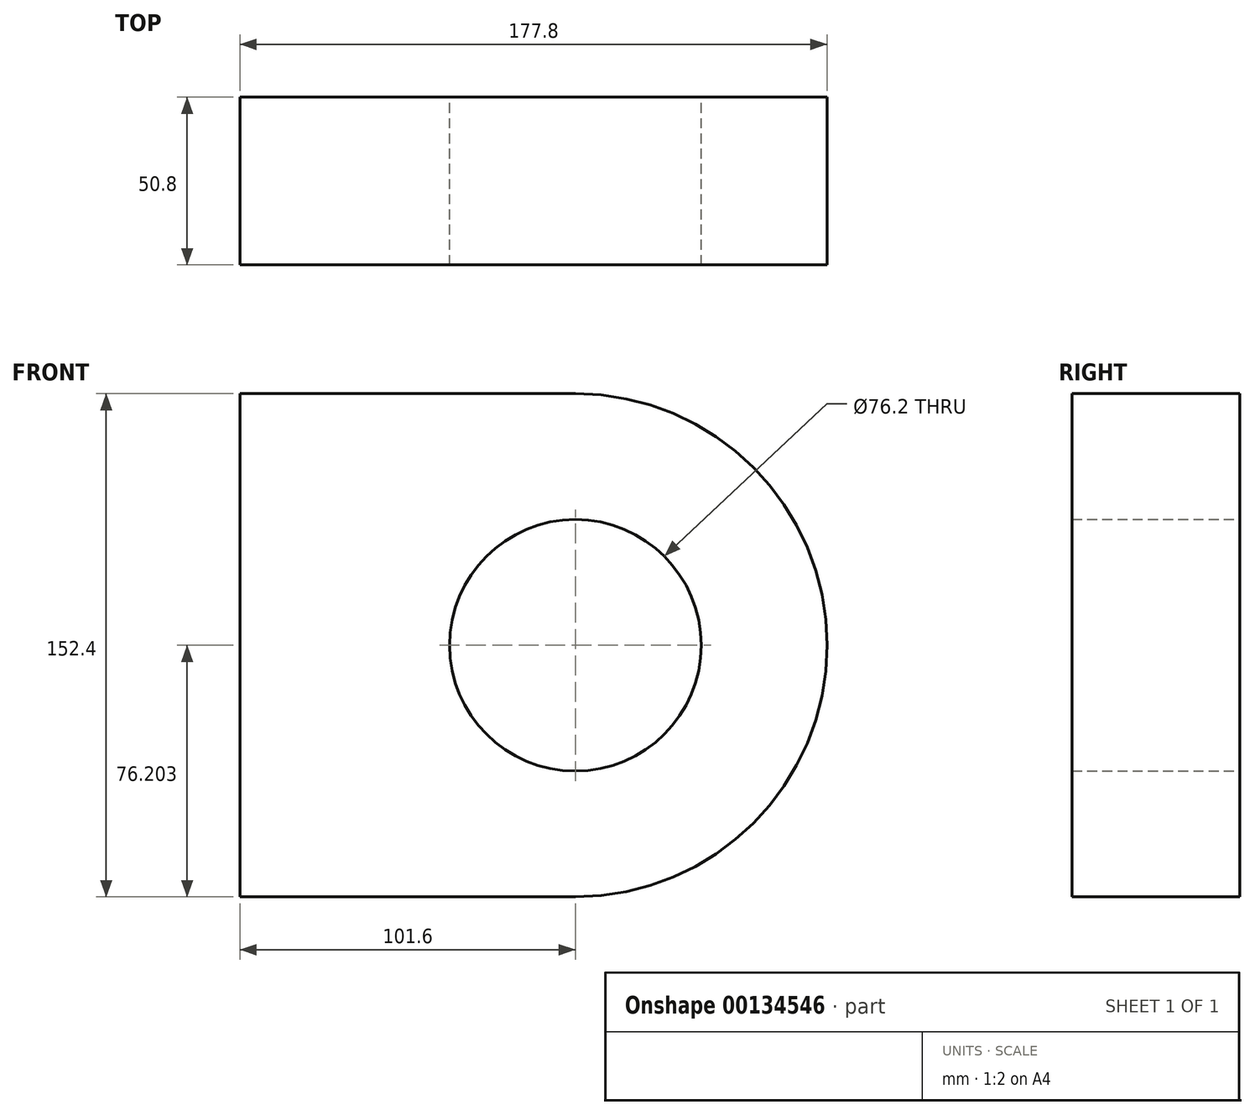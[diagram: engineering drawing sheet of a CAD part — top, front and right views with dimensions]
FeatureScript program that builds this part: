
annotation { "Feature Type Name" : "Feature", "Feature Type Description" : "" }
export const myFeature = defineFeature(function(context is Context, id is Id, definition is map)
    precondition{}
    {
        {
            var Q0;
            Q0=qCreatedBy(makeId("Front.planeOp"),FACE);
            var sketch = newSketch(context, id + "F0", { "sketchPlane" : qUnion([Q0])});
            skLineSegment(sketch, "E0", {"start": v(-101.6, 149.73) * mm, "end": v(-101.6, -2.67) * mm});
            skLineSegment(sketch, "E1", {"start": v(-101.6, -2.67) * mm, "end": v(0, -2.67) * mm});
            skLineSegment(sketch, "E2", {"start": v(-101.6, 149.73) * mm, "end": v(0, 149.73) * mm});
            skArc(sketch, "E3", {"start": v(0, -2.67) * mm, "mid": v(76.2, 73.53) * mm, "end": v(0, 149.73) * mm});
            skPoint(sketch, "E3.centerSnap0", {"position": v(-101.6, 73.53) * mm});
            skCircle(sketch, "E4", {"center": v(0, 73.53) * mm, "radius": 38.1 * mm});
            skSolve(sketch);
        }
        {
            var Q0;
            Q0=makeQuery(id+"F0.imprint","IMPRINT",FACE,{"disambiguationData":[TD([[makeQuery(id+"F0.imprint","IMPRINT",EDGE,{"derivedFrom":sQuery(id+"F0.wireOp",EDGE,"E0")}),1.0]])]});
            extrude(context, id + "F1", {"entities" : qUnion([Q0]), "depth" : 50.8 * mm});
        }
    });
